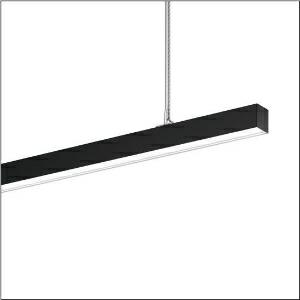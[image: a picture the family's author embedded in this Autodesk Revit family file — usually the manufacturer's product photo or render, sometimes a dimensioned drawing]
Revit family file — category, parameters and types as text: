
# Revit family: silica_r__21_51mx30tbt5b_11dd
name_source: partatom
category: Lighting Fixtures
units: mm (PartAtom-declared; Revit-internal decimal feet)

## family parameters
Cut with Voids When Loaded = No
Host = Face
Light Source = No
Part Type = Normal
Room Calculation Point = No
Round Connector Dimension = Use Diameter
Shared = No

## types (1)
- --- (1 x LED, 5150 lm, 42.2 W, 6500K)
    Apparent Load = 42 VA
    CIE Flux Codes = 47 79 96 58 100
    Color Rendering = 80
    Color Temperature = 6500K
    Default Elevation = 1800 mm
    Description = Silica® 21, office luminaire, primary optical cover: cover, of PMMA, opal, light emission: direct/indirect distribution, primary light characteristic: symmetric, installation type: suspended mounting, LED, rated luminous flux: 5.150lm, luminous efficacy: 116lm/W, light colour: 8tw, colour temperature: 2700..6500K, control gear: DALI DT8, with terminal, 3+2-pole, max. 2.5mm², mains connection: 220..240V, AC, 50/60Hz, rated input power: 44.3W, luminaire housing, of aluminium, matt jet black (RAL 9005), length: 1.504mm, width: 53mm, height: 53mm, protection rating (complete): IP20, insulation class (complete): insulation class I (protective earthing), certification: CE, permissible operating ambient temperature: 0..+35°C, standard: EN 50419, packaging unit: 1 piece
    Height = 53 mm
    Lamp = 1 x LED
    Lamp Light Flux = 5150 lm
    Lamp Power = 42.2 W
    Lamp count = 1
    Length = 1504 mm
    Luminous efficacy = 122 lm/W
    Manufacturer = Siteco
    ModVariant = No
    Model = 51MX30TBT5B
    Mounting Place = Ceiling
    Mounting Type = Pendant
    Number of Poles = 1
    OnlyDefault = Yes
    Power Factor = 1
    Product Name = Silica® 21
    Product group = office luminaire | ceiling pendant
    ProductGroupID = 904
    Protection Class = Protection class I
    Protection Degree = IP 20
    RLX_Detail_Level = 1
    RLX_Emergency_Light_Flux = 0 lm
    RLX_Emergency_Type = 0
    RLX_Emergency_Type_DB = No
    RlxData = <blob elided: 22897 chars, md5=c76d72cc>
    Socket = socket
    Standby Power = 0 W
    System Light Flux = 5150 lm
    System Power = 42 W
    Type Comments = individual setting
    Type Image = l_1335856.jpg
    URL = http://relux.com
    VarID = @adj_139632
    Voltage = 0 V
    Weight = 0.00 kg
    Width = 53 mm

## geometry (parser evidence)
native form markers: Blend x4, Sweep x11
no freeform markers — native parametric forms only
